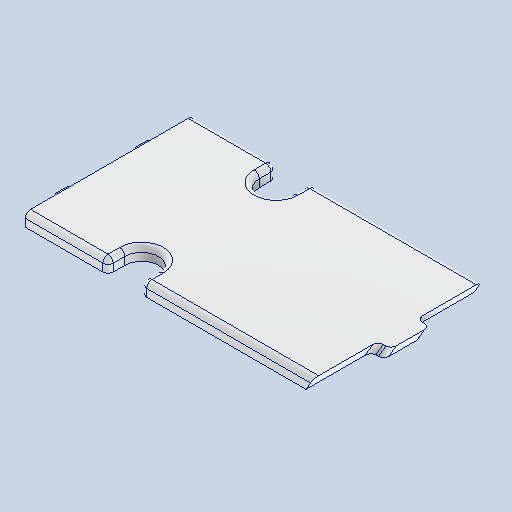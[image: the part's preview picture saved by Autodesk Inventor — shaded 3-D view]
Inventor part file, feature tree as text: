
AUTODESK INVENTOR PART (.ipt)
format: ipt  version: 2025 (Build 290162010, 162A)  size: 240,640 bytes
history: native  units: mm
features: reference x10, sketch x5, other x4, extrude x3, sweep x1, fillet x1
ambient origin geometry x8: Origin, YZ Plane, XZ Plane, XY Plane, X Axis, Y Axis, Z Axis, Center Point
bodies: Volumenkörper1 (feature_tree)
feature tree (24):
  extrude  "Extrusion1"  Depth=2.5mm
  extrude  "Extrusion3"  Depth=2.5mm
  sweep  "Sweeping2"
  fillet  "Rundung3"  Radius=10.0mm
  extrude  "Extrusion4"  Depth=2.0mm
  sketch  "Skizze1"  dims[d0=5.0mm d1=0.0mm d7=2.5mm]
  reference  "Referenz35"
  reference  "Referenz37"
  sketch  "Skizze5"  dims[d8=5.0mm d9=2.5mm]
  reference  "Referenz54"
  reference  "Referenz55"
  reference  "Referenz56"
  reference  "Referenz57"
  reference  "Referenz58"
  reference  "Referenz59"
  sketch  "Skizze6"  dims[d10=5.0mm d11=3.0mm d12=0.0mm d14=10.0mm]
  sketch  "Skizze7"  dims[d15=0.0mm d16=0.0mm d17=2.0mm]
  sketch  "Skizze8"  dims[d18=3.3mm d19=0.0mm d4=0.0mm d5=0.0mm d6=0.0mm]
  reference  "Referenz61"
  reference  "Referenz62"
  other  "<userpath>\Documents\Inventor\Krandemonstrator\Schlitten.iam"
  other  "Schlitten.iam"
  other  "SchlittenS:1"
  other  "SchlittenDeckel:1"
